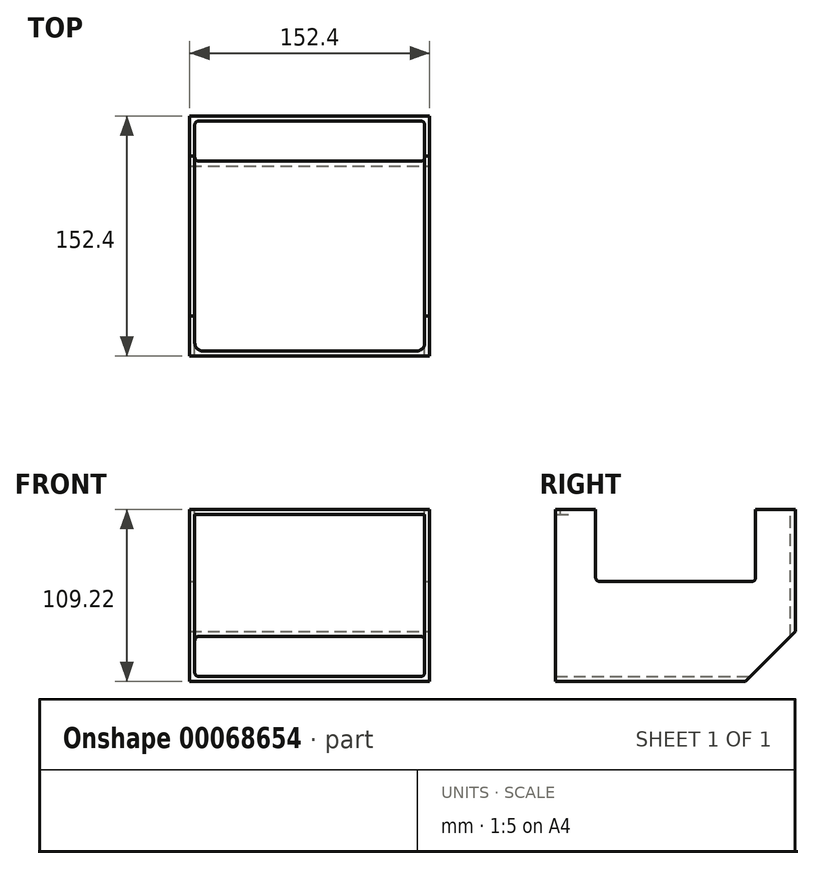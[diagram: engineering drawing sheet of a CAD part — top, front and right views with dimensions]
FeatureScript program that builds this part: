
annotation { "Feature Type Name" : "Feature", "Feature Type Description" : "" }
export const myFeature = defineFeature(function(context is Context, id is Id, definition is map)
    precondition{}
    {
        {
            var Q0;
            Q0=qCreatedBy(makeId("Front.planeOp"),FACE);
            var sketch = newSketch(context, id + "F0", { "sketchPlane" : qUnion([Q0])});
            skLineSegment(sketch, "E0.bottom", {"start": v(0, 0) * mm, "end": v(152.4, 0) * mm});
            skLineSegment(sketch, "E0.top", {"start": v(0, 109.22) * mm, "end": v(152.4, 109.22) * mm});
            skLineSegment(sketch, "E0.left", {"start": v(0, 0) * mm, "end": v(0, 109.22) * mm});
            skLineSegment(sketch, "E0.right", {"start": v(152.4, 0) * mm, "end": v(152.4, 109.22) * mm});
            skSolve(sketch);
        }
        {
            var Q0;
            Q0=makeQuery(id+"F0.imprint","IMPRINT",FACE,{"disambiguationData":[TD([[makeQuery(id+"F0.imprint","IMPRINT",EDGE,{"derivedFrom":sQuery(id+"F0.wireOp",EDGE,"E0.bottom")}),1.0]])]});
            extrude(context, id + "F1", {"entities" : qUnion([Q0]), "depth" : 152.4 * mm});
        }
        {
            var Q0;
            Q0=makeQuery(id+"F1.opExtrude","CAP_FACE",FACE,{"disambiguationData":[OSD([sQuery(id+"F0.wireOp",EDGE,"E0.bottom"),sQuery(id+"F0.wireOp",EDGE,"E0.top"),sQuery(id+"F0.wireOp",EDGE,"E0.left"),sQuery(id+"F0.wireOp",EDGE,"E0.right")])],"isStart":false});
            shell(context, id + "F2", {"entities" : qUnion([Q0]), "thickness" : 3.17 * mm});
        }
        {
            var Q0;
            Q0=makeQuery(id+"F1.opExtrude","SWEPT_FACE",FACE,{"disambiguationData":[OSD([sQuery(id+"F0.wireOp",EDGE,"E0.right")])]});
            var sketch = newSketch(context, id + "F3", { "sketchPlane" : qUnion([Q0])});
            skLineSegment(sketch, "E1.bottom", {"start": v(-127, 109.22) * mm, "end": v(-25.4, 109.22) * mm});
            skLineSegment(sketch, "E1.top", {"start": v(-127, 63.5) * mm, "end": v(-25.4, 63.5) * mm});
            skLineSegment(sketch, "E1.left", {"start": v(-127, 109.22) * mm, "end": v(-127, 63.5) * mm});
            skLineSegment(sketch, "E1.right", {"start": v(-25.4, 109.22) * mm, "end": v(-25.4, 63.5) * mm});
            skSolve(sketch);
        }
        {
            var Q0;
            Q0=makeQuery(id+"F3.imprint","IMPRINT",FACE,{"disambiguationData":[TD([[makeQuery(id+"F3.imprint","IMPRINT",EDGE,{"derivedFrom":sQuery(id+"F3.wireOp",EDGE,"E1.bottom")}),-1.0]])]});
            extrude(context, id + "F4", {"entities" : qUnion([Q0]), "operationType" : NewBodyOperationType.REMOVE, "endBound" : BoundingType.THROUGH_ALL, "oppositeDirection" : true, "depth" : 25.4 * mm});
        }
        {
            var Q0;
            {var subQ2=sQuery(id+"F0.wireOp",EDGE,"E0.top");Q0=makeQuery(id+"F4.boolean.opBoolean","SPLIT",FACE,{"disambiguationData":[TD([makeQuery(id+"F4.opExtrude","SWEPT_FACE",FACE,{"disambiguationData":[OSD([sQuery(id+"F3.wireOp",EDGE,"E1.left")])]})])],"derivedFrom":makeQuery(id+"F1.opExtrude","SWEPT_FACE",FACE,{"disambiguationData":[OSD([subQ2])]})});}
            var sketch = newSketch(context, id + "F5", { "sketchPlane" : qUnion([Q0])});
            skLineSegment(sketch, "E2.bottom", {"start": v(149.22, -149.22) * mm, "end": v(3.18, -149.22) * mm});
            skLineSegment(sketch, "E2.top", {"start": v(149.22, -3.17) * mm, "end": v(3.17, -3.18) * mm});
            skLineSegment(sketch, "E2.left", {"start": v(149.22, -149.22) * mm, "end": v(149.22, -3.17) * mm});
            skLineSegment(sketch, "E2.right", {"start": v(3.18, -149.22) * mm, "end": v(3.17, -3.18) * mm});
            skSolve(sketch);
        }
        {
            var Q0;
            {var subQ0=sQuery(id+"F5.wireOp",EDGE,"E2.bottom");Q0=makeQuery(id+"F5.imprint","IMPRINT",FACE,{"disambiguationData":[TD([[makeQuery(id+"F5.imprint","IMPRINT",EDGE,{"derivedFrom":subQ0}),-1.0]])]});}
            var Q1;
            {var subQ0=sQuery(id+"F5.wireOp",EDGE,"E2.top");Q1=makeQuery(id+"F5.imprint","IMPRINT",FACE,{"disambiguationData":[TD([[makeQuery(id+"F5.imprint","IMPRINT",EDGE,{"derivedFrom":subQ0}),1.0]])]});}
            extrude(context, id + "F6", {"entities" : qUnion([Q0, Q1]), "operationType" : NewBodyOperationType.REMOVE, "oppositeDirection" : true, "depth" : 25.4 * mm});
        }
        {
            var Q0;
            Q0=makeQuery(id+"F1.opExtrude","SWEPT_FACE",FACE,{"disambiguationData":[OSD([sQuery(id+"F0.wireOp",EDGE,"E0.right")])]});
            var sketch = newSketch(context, id + "F7", { "sketchPlane" : qUnion([Q0])});
            skLineSegment(sketch, "E3", {"start": v(0, 0) * mm, "end": v(-31.75, 0) * mm});
            skLineSegment(sketch, "E4", {"start": v(-31.75, 0) * mm, "end": v(0, 31.75) * mm});
            skLineSegment(sketch, "E5", {"start": v(0, 0) * mm, "end": v(0, 31.75) * mm});
            skSolve(sketch);
        }
        {
            var Q0;
            Q0=makeQuery(id+"F7.imprint","IMPRINT",FACE,{"disambiguationData":[TD([[makeQuery(id+"F7.imprint","IMPRINT",EDGE,{"derivedFrom":sQuery(id+"F7.wireOp",EDGE,"E3")}),1.0]])]});
            extrude(context, id + "F8", {"entities" : qUnion([Q0]), "operationType" : NewBodyOperationType.REMOVE, "endBound" : BoundingType.THROUGH_ALL, "oppositeDirection" : true, "depth" : 25.4 * mm});
        }
        {
            var Q0;
            Q0=makeQuery(id+"F2.opShell","OFFSET_EDGE",EDGE,{"disambiguationData":[OSD([sQuery(id+"F0.wireOp",EDGE,"E0.bottom"),sQuery(id+"F0.wireOp",EDGE,"E0.left")])]});
            var Q1;
            {var subQ0=sQuery(id+"F0.wireOp",EDGE,"E0.left");Q1=makeQuery(id+"F6.boolean.opBoolean","MERGE",EDGE,{"derivedFrom":[makeQuery(id+"F2.opShell","OFFSET_EDGE",EDGE,{"disambiguationData":[OSD([subQ0]),TDD([makeQuery(id+"F1.opExtrude","CAP_EDGE",EDGE,{"disambiguationData":[OSD([subQ0])],"isStart":true})])]}),makeQuery(id+"F6.opExtrude","SWEPT_EDGE",EDGE,{"disambiguationData":[OSD([sQuery(id+"F5.wireOp",EDGE,"E2.top"),sQuery(id+"F5.wireOp",EDGE,"E2.right")])]})]});}
            var Q2;
            {var subQ0=sQuery(id+"F0.wireOp",EDGE,"E0.right");Q2=makeQuery(id+"F6.boolean.opBoolean","MERGE",EDGE,{"derivedFrom":[makeQuery(id+"F2.opShell","OFFSET_EDGE",EDGE,{"disambiguationData":[OSD([subQ0]),TDD([makeQuery(id+"F1.opExtrude","CAP_EDGE",EDGE,{"disambiguationData":[OSD([subQ0])],"isStart":true})])]}),makeQuery(id+"F6.opExtrude","SWEPT_EDGE",EDGE,{"disambiguationData":[OSD([sQuery(id+"F5.wireOp",EDGE,"E2.top"),sQuery(id+"F5.wireOp",EDGE,"E2.left")])]})]});}
            var Q3;
            Q3=makeQuery(id+"F4.boolean.opBoolean","COPY",EDGE,{"disambiguationData":[OD(0.0)],"derivedFrom":makeQuery(id+"F4.opExtrude","SWEPT_EDGE",EDGE,{"disambiguationData":[OSD([sQuery(id+"F3.wireOp",EDGE,"E1.top"),sQuery(id+"F3.wireOp",EDGE,"E1.right")])]})});
            var Q4;
            Q4=makeQuery(id+"F4.boolean.opBoolean","COPY",EDGE,{"disambiguationData":[OD(1.0)],"derivedFrom":makeQuery(id+"F4.opExtrude","SWEPT_EDGE",EDGE,{"disambiguationData":[OSD([sQuery(id+"F3.wireOp",EDGE,"E1.top"),sQuery(id+"F3.wireOp",EDGE,"E1.right")])]})});
            var Q5;
            Q5=makeQuery(id+"F4.boolean.opBoolean","COPY",EDGE,{"disambiguationData":[OD(1.0)],"derivedFrom":makeQuery(id+"F4.opExtrude","SWEPT_EDGE",EDGE,{"disambiguationData":[OSD([sQuery(id+"F3.wireOp",EDGE,"E1.top"),sQuery(id+"F3.wireOp",EDGE,"E1.left")])]})});
            var Q6;
            Q6=makeQuery(id+"F4.boolean.opBoolean","COPY",EDGE,{"disambiguationData":[OD(0.0)],"derivedFrom":makeQuery(id+"F4.opExtrude","SWEPT_EDGE",EDGE,{"disambiguationData":[OSD([sQuery(id+"F3.wireOp",EDGE,"E1.top"),sQuery(id+"F3.wireOp",EDGE,"E1.left")])]})});
            var Q7;
            Q7=makeQuery(id+"F2.opShell","OFFSET_EDGE",EDGE,{"disambiguationData":[OSD([sQuery(id+"F0.wireOp",EDGE,"E0.bottom"),sQuery(id+"F0.wireOp",EDGE,"E0.right")])]});
            fillet(context, id + "F9", {"entities" : qUnion([Q0, Q1, Q2, Q3, Q4, Q5, Q6, Q7]), "radius" : 2.54 * mm, "tangentPropagation" : true, "allowEdgeOverflow" : false});
        }
        {
            var Q0;
            Q0=makeQuery(id+"F6.boolean.opBoolean","COPY",EDGE,{"derivedFrom":makeQuery(id+"F6.opExtrude","SWEPT_EDGE",EDGE,{"disambiguationData":[OSD([sQuery(id+"F5.wireOp",EDGE,"E2.bottom"),sQuery(id+"F5.wireOp",EDGE,"E2.right")])]})});
            var Q1;
            Q1=makeQuery(id+"F6.boolean.opBoolean","COPY",EDGE,{"derivedFrom":makeQuery(id+"F6.opExtrude","SWEPT_EDGE",EDGE,{"disambiguationData":[OSD([sQuery(id+"F5.wireOp",EDGE,"E2.bottom"),sQuery(id+"F5.wireOp",EDGE,"E2.left")])]})});
            fillet(context, id + "F10", {"entities" : qUnion([Q0, Q1]), "radius" : 5.08 * mm, "tangentPropagation" : true, "allowEdgeOverflow" : false});
        }
    });
